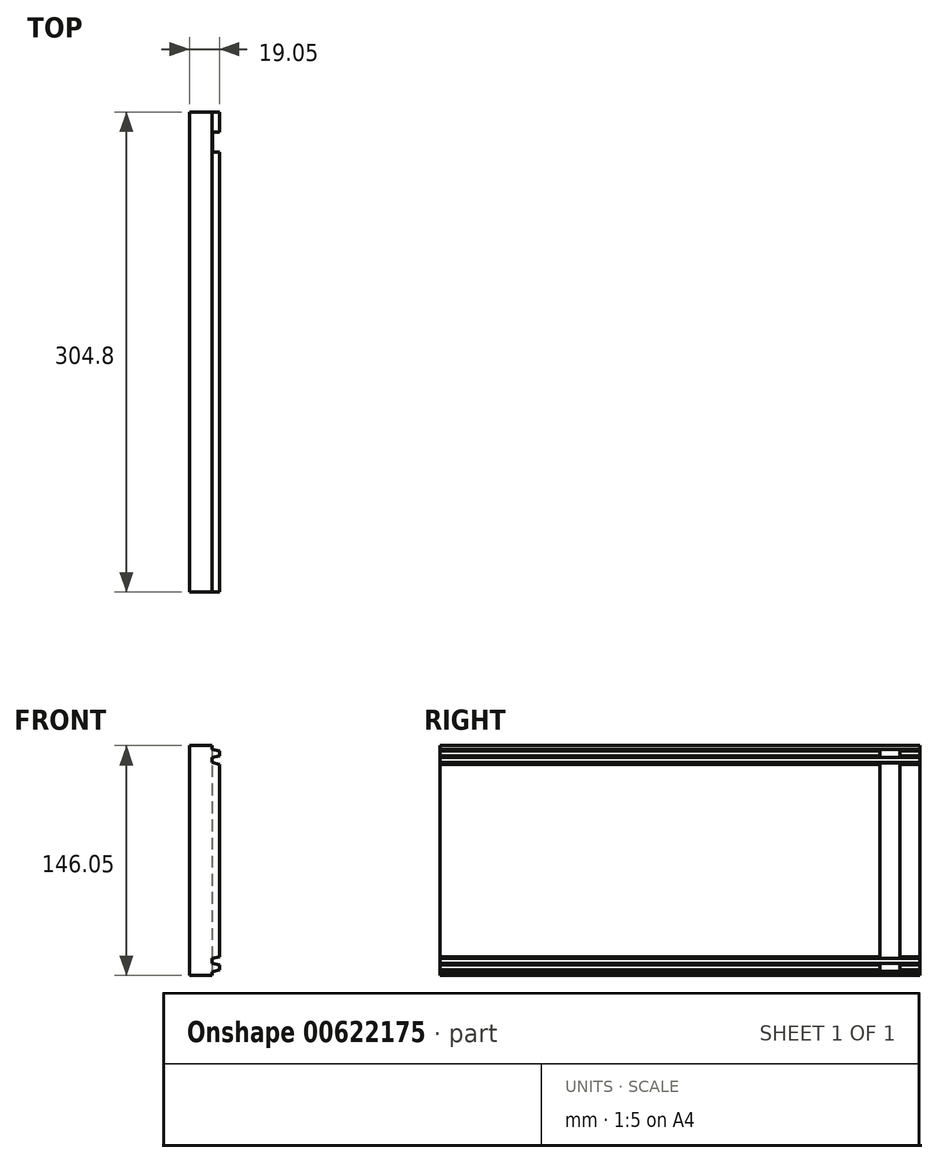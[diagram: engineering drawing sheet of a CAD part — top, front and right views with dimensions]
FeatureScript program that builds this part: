
annotation { "Feature Type Name" : "Feature", "Feature Type Description" : "" }
export const myFeature = defineFeature(function(context is Context, id is Id, definition is map)
    precondition{}
    {
        {
            var Q0;
            Q0=qCreatedBy(makeId("Front.planeOp"),FACE);
            var sketch = newSketch(context, id + "F0", { "sketchPlane" : qUnion([Q0])});
            skLineSegment(sketch, "E0.bottom", {"start": v(0, 0) * mm, "end": v(19.05, 0) * mm});
            skLineSegment(sketch, "E0.top", {"start": v(0, 146.05) * mm, "end": v(19.05, 146.05) * mm});
            skLineSegment(sketch, "E0.left", {"start": v(0, 0) * mm, "end": v(0, 146.05) * mm});
            skLineSegment(sketch, "E0.right", {"start": v(19.05, 0) * mm, "end": v(19.05, 146.05) * mm});
            skSolve(sketch);
        }
        {
            var Q0;
            Q0 = qSketchRegion(id + "F0", true);
            extrude(context, id + "F1", {"entities" : qUnion([Q0]), "depth" : 304.8 * mm, "offsetDistance" : 25.4 * mm});
        }
        {
            var Q0;
            Q0=qCreatedBy(makeId("Front.planeOp"),FACE);
            cPlane(context, id + "F2", {"entities" : qUnion([Q0]), "cplaneType" : CPlaneType.OFFSET, "offset" : 25.4 * mm, "width" : 152.4 * mm, "height" : 152.4 * mm});
        }
        {
            var Q0;
            Q0=qCreatedBy(makeId("Front.planeOp"),FACE);
            var sketch = newSketch(context, id + "F3", { "sketchPlane" : qUnion([Q0])});
            skLineSegment(sketch, "E1", {"start": v(24.14, 124.61) * mm, "end": v(24.14, 153.19) * mm});
            skLineSegment(sketch, "E2.MirrorCS", {"start": v(14.29, 138.37) * mm, "end": v(14.29, 135.2) * mm});
            skLineSegment(sketch, "E3.MirrorCS", {"start": v(19.05, 124.61) * mm, "end": v(24.14, 124.61) * mm});
            skLineSegment(sketch, "E4.MirrorCS", {"start": v(19.05, 142.6) * mm, "end": v(19.05, 139.43) * mm});
            skLineSegment(sketch, "E5.MirrorCS", {"start": v(14.29, 135.2) * mm, "end": v(19.05, 134.14) * mm});
            skLineSegment(sketch, "E6.MirrorCS", {"start": v(19.05, 134.14) * mm, "end": v(19.05, 124.61) * mm});
            skLineSegment(sketch, "E7.MirrorCS", {"start": v(19.05, 139.43) * mm, "end": v(14.29, 138.37) * mm});
            skLineSegment(sketch, "E8.MirrorCS", {"start": v(14.29, 143.66) * mm, "end": v(19.05, 142.6) * mm});
            skLineSegment(sketch, "E9.MirrorCS", {"start": v(14.29, 153.19) * mm, "end": v(14.29, 143.66) * mm});
            skLineSegment(sketch, "E10.MirrorCS", {"start": v(24.14, 153.19) * mm, "end": v(14.29, 153.19) * mm});
            skLineSegment(sketch, "E11", {"start": v(24.14, 153.19) * mm, "end": v(24.14, 124.61) * mm});
            skPoint(sketch, "E12", {"position": v(24.14, 138.9) * mm});
            skPoint(sketch, "E13", {"position": v(19.05, 142.6) * mm});
            skSolve(sketch);
        }
        {
            var Q0;
            Q0 = qSketchRegion(id + "F3", true);
            extrude(context, id + "F4", {"entities" : qUnion([Q0]), "operationType" : NewBodyOperationType.REMOVE, "depth" : 304.8 * mm, "offsetDistance" : 25.4 * mm});
        }
        {
            var Q0;
            Q0=qCreatedBy(makeId("Front.planeOp"),FACE);
            var sketch = newSketch(context, id + "F5", { "sketchPlane" : qUnion([Q0])});
            skLineSegment(sketch, "E14", {"start": v(24.14, 21.44) * mm, "end": v(24.14, -7.14) * mm});
            skLineSegment(sketch, "E15", {"start": v(24.14, -7.14) * mm, "end": v(14.29, -7.14) * mm});
            skLineSegment(sketch, "E16", {"start": v(14.29, -7.14) * mm, "end": v(14.29, 2.39) * mm});
            skLineSegment(sketch, "E17", {"start": v(14.29, 2.39) * mm, "end": v(19.05, 3.45) * mm});
            skLineSegment(sketch, "E18", {"start": v(19.05, 3.45) * mm, "end": v(19.05, 6.62) * mm});
            skLineSegment(sketch, "E19", {"start": v(19.05, 6.62) * mm, "end": v(14.29, 7.68) * mm});
            skLineSegment(sketch, "E20", {"start": v(14.29, 7.68) * mm, "end": v(14.29, 10.85) * mm});
            skLineSegment(sketch, "E21", {"start": v(14.29, 10.85) * mm, "end": v(19.05, 11.91) * mm});
            skLineSegment(sketch, "E22", {"start": v(19.05, 11.91) * mm, "end": v(19.05, 21.44) * mm});
            skLineSegment(sketch, "E23", {"start": v(19.05, 21.44) * mm, "end": v(24.14, 21.44) * mm});
            skPoint(sketch, "E24.positionSnap0", {"position": v(24.14, 7.15) * mm});
            skPoint(sketch, "E25", {"position": v(19.05, 3.45) * mm});
            skSolve(sketch);
        }
        {
            var Q0;
            Q0 = qSketchRegion(id + "F5", true);
            extrude(context, id + "F6", {"entities" : qUnion([Q0]), "operationType" : NewBodyOperationType.REMOVE, "depth" : 304.8 * mm, "offsetDistance" : 25.4 * mm});
        }
        {
            var Q0;
            Q0=qCreatedBy(id+"F2.planeOp",FACE);
            var sketch = newSketch(context, id + "F7", { "sketchPlane" : qUnion([Q0])});
            skLineSegment(sketch, "E26.bottom", {"start": v(27.5, 0) * mm, "end": v(14.8, 0) * mm});
            skLineSegment(sketch, "E26.top", {"start": v(27.5, 146.05) * mm, "end": v(14.8, 146.05) * mm});
            skLineSegment(sketch, "E26.left", {"start": v(27.5, 0) * mm, "end": v(27.5, 146.05) * mm});
            skLineSegment(sketch, "E26.right", {"start": v(14.8, 0) * mm, "end": v(14.8, 146.05) * mm});
            skSolve(sketch);
        }
        {
            var Q0;
            Q0 = qSketchRegion(id + "F7", true);
            extrude(context, id + "F8", {"entities" : qUnion([Q0]), "operationType" : NewBodyOperationType.REMOVE, "oppositeDirection" : true, "depth" : 12.7 * mm, "offsetDistance" : 25.4 * mm});
        }
    });
